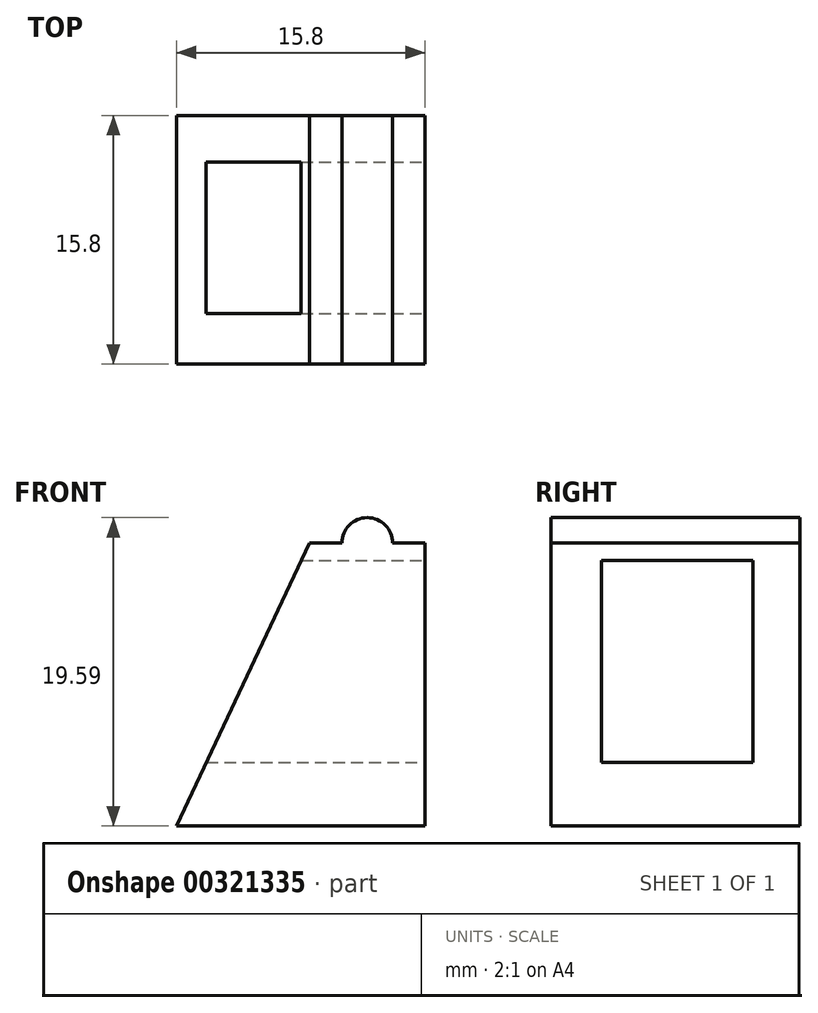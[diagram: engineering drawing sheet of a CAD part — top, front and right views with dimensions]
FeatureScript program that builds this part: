
annotation { "Feature Type Name" : "Feature", "Feature Type Description" : "" }
export const myFeature = defineFeature(function(context is Context, id is Id, definition is map)
    precondition{}
    {
        {
            var Q0;
            Q0=qCreatedBy(makeId("Front.planeOp"),FACE);
            var sketch = newSketch(context, id + "F0", { "sketchPlane" : qUnion([Q0])});
            skLineSegment(sketch, "E0", {"start": v(-16.88, 29.54) * mm, "end": v(-24.23, 29.54) * mm});
            skLineSegment(sketch, "E1", {"start": v(-24.23, 29.54) * mm, "end": v(-32.68, 11.56) * mm});
            skLineSegment(sketch, "E2", {"start": v(-32.68, 11.56) * mm, "end": v(-16.88, 11.56) * mm});
            skLineSegment(sketch, "E3", {"start": v(-16.88, 11.56) * mm, "end": v(-16.88, 29.54) * mm});
            skCircle(sketch, "E4", {"center": v(-20.55, 29.54) * mm, "radius": 1.61 * mm});
            skSolve(sketch);
        }
        {
            var Q0;
            Q0 = qSketchRegion(id + "F0", true);
            extrude(context, id + "F1", {"entities" : qUnion([Q0]), "oppositeDirection" : true, "depth" : 15.8 * mm});
        }
        {
            var Q0;
            Q0=qCreatedBy(makeId("Right.planeOp"),FACE);
            var sketch = newSketch(context, id + "F2", { "sketchPlane" : qUnion([Q0])});
            skLineSegment(sketch, "E5", {"start": v(12.82, 28.42) * mm, "end": v(12.82, 15.6) * mm});
            skLineSegment(sketch, "E6", {"start": v(12.82, 15.6) * mm, "end": v(3.2, 15.6) * mm});
            skLineSegment(sketch, "E7", {"start": v(3.2, 15.6) * mm, "end": v(3.2, 28.42) * mm});
            skLineSegment(sketch, "E8", {"start": v(12.82, 28.42) * mm, "end": v(3.2, 28.42) * mm});
            skSolve(sketch);
        }
        {
            var Q0;
            Q0 = qSketchRegion(id + "F2", true);
            extrude(context, id + "F3", {"entities" : qUnion([Q0]), "operationType" : NewBodyOperationType.REMOVE, "oppositeDirection" : true, "depth" : 55 * mm});
        }
    });
